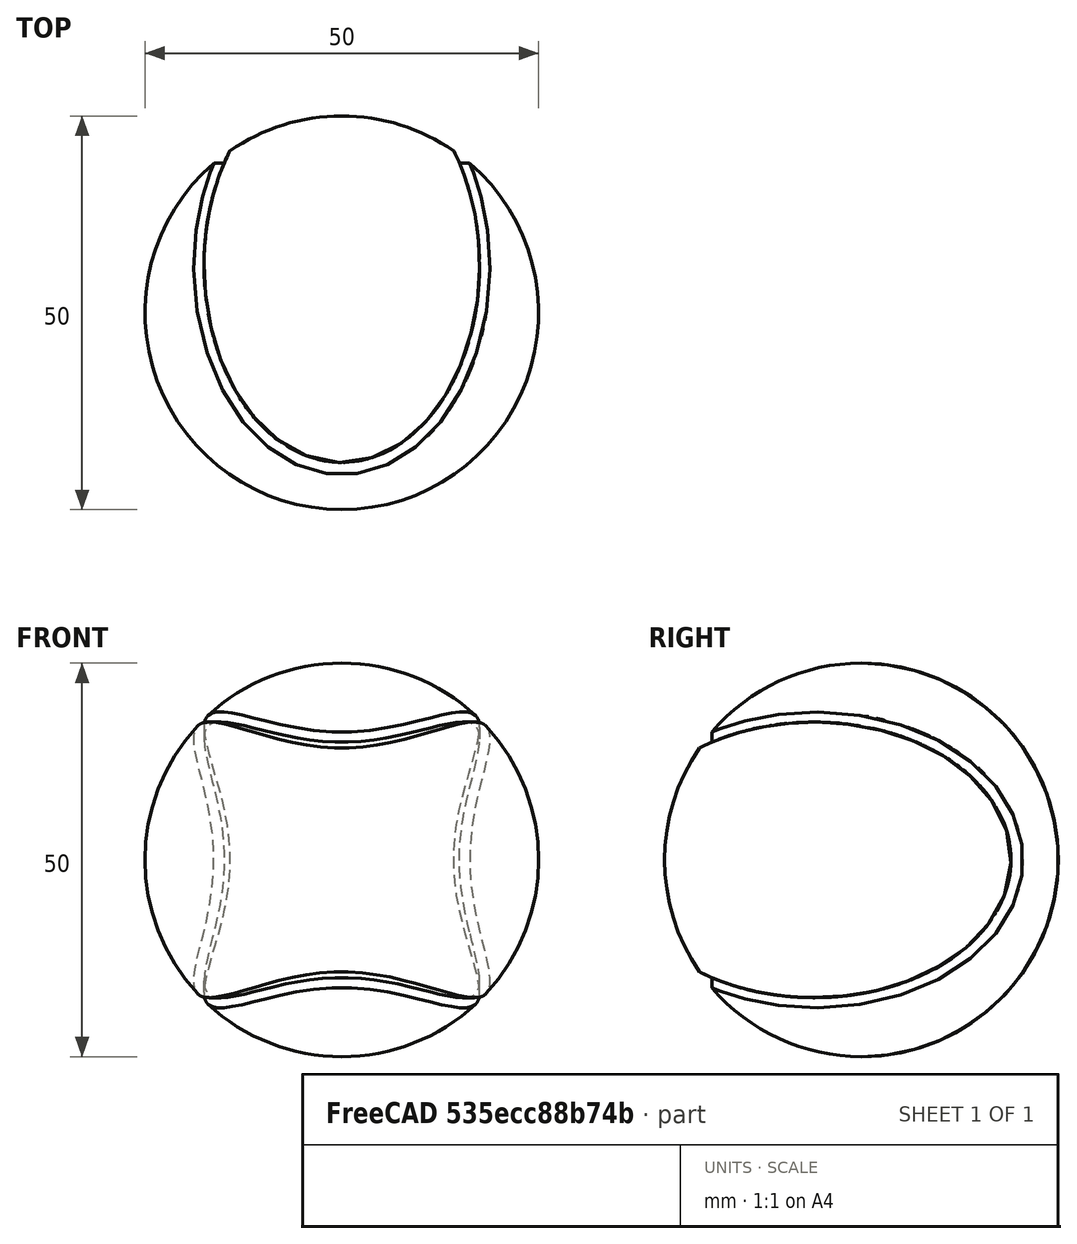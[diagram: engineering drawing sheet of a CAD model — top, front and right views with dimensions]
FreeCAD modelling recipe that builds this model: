
FCSTD DOCUMENT  (FreeCAD 0.19R16207 (Git))
Label: BOLA TENIS_1
License: CreativeCommons Attribution-NonCommercial-ShareAlike
LicenseURL: http://creativecommons.org/licenses/by-nc-sa/4.0/
objects: Part::Sphere×2, Part::Cut×2, Part::Ellipse×1, Part::Extrusion×1, Part::FeaturePython×1, Part::MultiCommon×1
note: 8 computed .brp shape members not serialized (recipe doc carries the construction recipe); baked Part::Feature solids carry a one-line shape summary decoded from their .brp

FEATURE [Part::Ellipse] Ellipse
  Angle0 = 0
  Angle1 = 360
  AttacherType = Attacher::AttachEngine3D
  MajorRadius = 25
  MinorRadius = 17.5
FEATURE [Part::Extrusion] Extrude
  Base = -> Ellipse
  Dir = (0,0,1)
  DirMode = 2
  FaceMakerClass = Part::FaceMakerBullseye
  LengthFwd = 55
  LengthRev = 0
  Placement = pos=(6,0,0) rot=(0,0,1;0rad)
  Solid = true
  Symmetric = true
FEATURE [Part::Sphere] Sphere
  Angle1 = -90
  Angle2 = 90
  Angle3 = 360
  AttacherType = Attacher::AttachEngine3D
  Radius = 25
FEATURE [Part::Cut] Cut
  Base = -> Sphere
  Tool = -> Extrude
FEATURE [Part::FeaturePython] Clone  label="Cut001"  # Draft clone (typed FeaturePython)
  AttacherType = Attacher::AttachEngine3D
  Fuse = false
  Objects = -> [Cut]
  Placement = pos=(0,0,0) rot=(0,-0.707107,0.707107;3.14159rad)
  Scale = (1,1,1)
FEATURE [Part::MultiCommon] Common
  Shapes = -> [Cut,Clone]
FEATURE [Part::Sphere] Sphere001
  Angle1 = -90
  Angle2 = 90
  Angle3 = 360
  AttacherType = Attacher::AttachEngine3D
  Radius = 25
FEATURE [Part::Cut] Cut001  label="Cut002"
  Base = -> Sphere001
  Placement = pos=(0,0,0) rot=(0,0,-1;4.71239rad)
  Tool = -> Common
